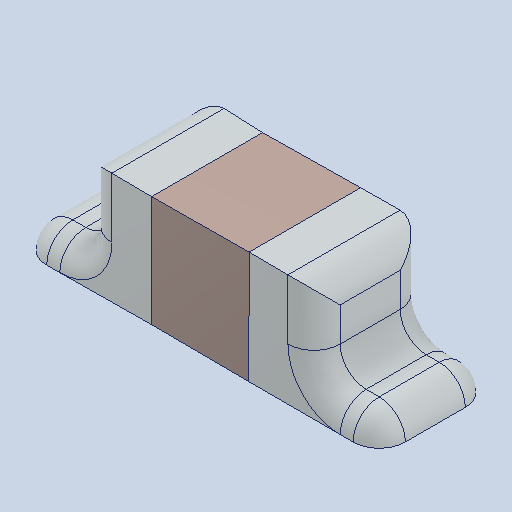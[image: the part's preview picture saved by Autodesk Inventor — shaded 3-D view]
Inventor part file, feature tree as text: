
AUTODESK INVENTOR PART (.ipt)
format: ipt  version: 2024 (Build 280153000, 153)  size: 148,992 bytes
history: native  units: in
note: dims shown in document units (in); Inventor stores cm internally (conversion verified against a paired STEP export)
features: mirror x1
ambient origin geometry x8: Origin, YZ Plane, XZ Plane, XY Plane, X Axis, Y Axis, Z Axis, Center Point
bodies: Solid1 (feature_tree)
feature tree (1):
  mirror  "Mirror1"
